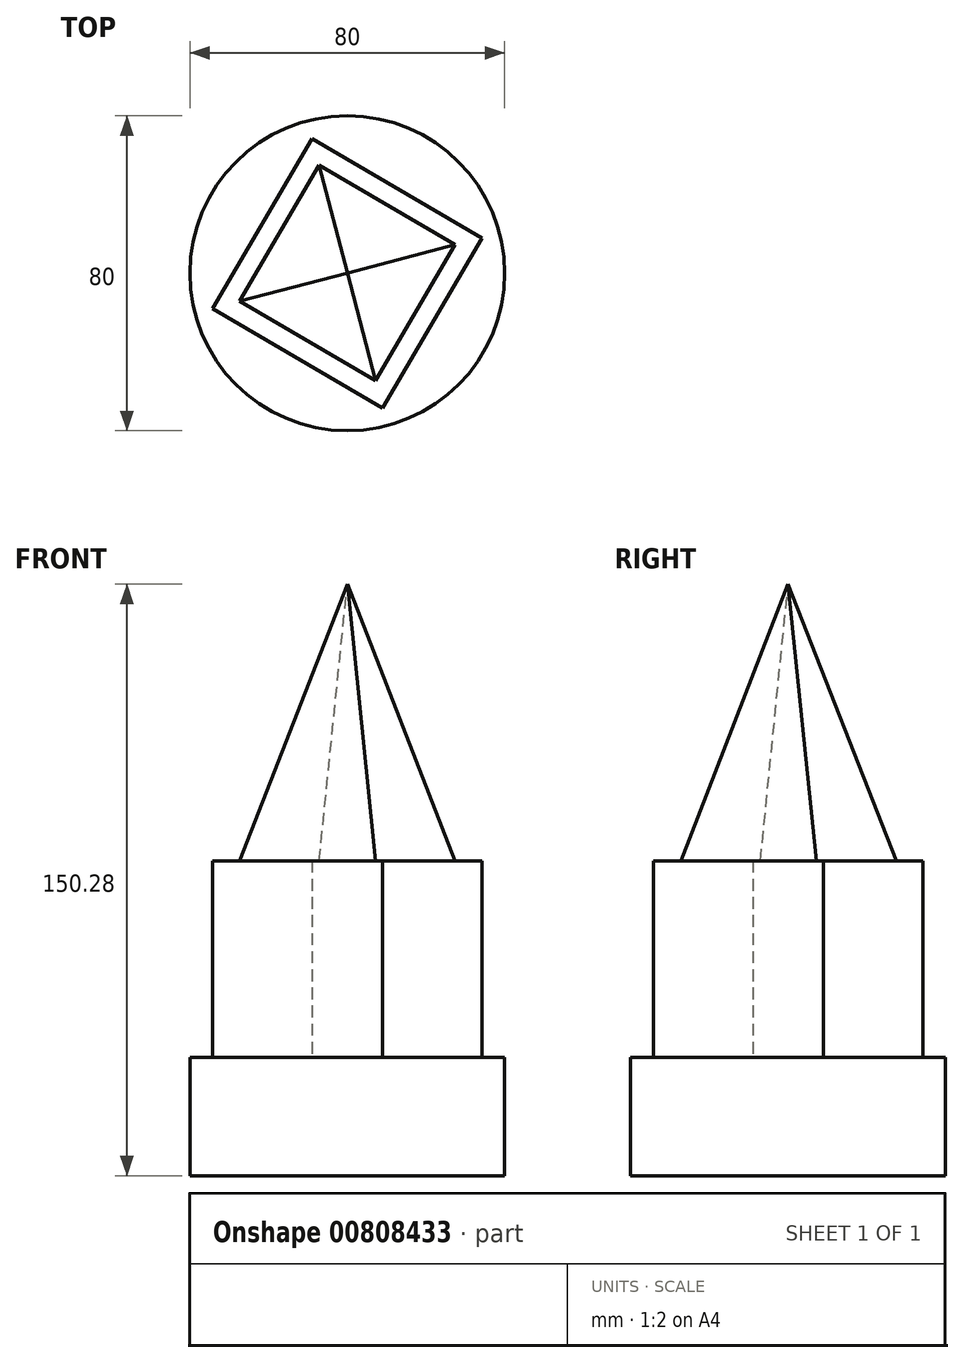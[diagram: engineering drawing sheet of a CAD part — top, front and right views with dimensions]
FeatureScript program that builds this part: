
annotation { "Feature Type Name" : "Feature", "Feature Type Description" : "" }
export const myFeature = defineFeature(function(context is Context, id is Id, definition is map)
    precondition{}
    {
        {
            var Q0;
            Q0=qCreatedBy(makeId("Top.planeOp"),FACE);
            var sketch = newSketch(context, id + "F0", { "sketchPlane" : qUnion([Q0])});
            skCircle(sketch, "E0", {"center": v(0, 0) * mm, "radius": 40 * mm});
            skSolve(sketch);
        }
        {
            var Q0;
            Q0 = qSketchRegion(id + "F0", true);
            extrude(context, id + "F1", {"entities" : qUnion([Q0]), "depth" : 30 * mm, "offsetDistance" : 25.4 * mm});
        }
        {
            var Q0;
            Q0=makeQuery(id+"F1.opExtrude","CAP_FACE",FACE,{"disambiguationData":[OSD([sQuery(id+"F0.wireOp",EDGE,"E0")])],"isStart":false});
            var sketch = newSketch(context, id + "F2", { "sketchPlane" : qUnion([Q0])});
            skCircle(sketch, "E1.cCircle", {"center": v(0, 0) * mm, "radius": 25 * mm, "construction": true});
            skLineSegment(sketch, "E1.0", {"start": v(-8.96, 34.2) * mm, "end": v(34.2, 8.96) * mm});
            skLineSegment(sketch, "E1.1", {"start": v(34.2, 8.96) * mm, "end": v(8.96, -34.2) * mm});
            skLineSegment(sketch, "E1.2", {"start": v(8.96, -34.2) * mm, "end": v(-34.2, -8.96) * mm});
            skLineSegment(sketch, "E1.3", {"start": v(-34.2, -8.96) * mm, "end": v(-8.96, 34.2) * mm});
            skPoint(sketch, "E1.0.midPoint", {"position": v(12.62, 21.58) * mm});
            skSolve(sketch);
        }
        {
            var Q0;
            Q0 = qSketchRegion(id + "F2", true);
            extrude(context, id + "F3", {"entities" : qUnion([Q0]), "operationType" : NewBodyOperationType.ADD, "depth" : 50 * mm, "offsetDistance" : 25.4 * mm});
        }
        {
            var Q0;
            Q0=makeQuery(id+"F3.opExtrude","CAP_FACE",FACE,{"disambiguationData":[OSD([sQuery(id+"F2.wireOp",EDGE,"E1.0"),sQuery(id+"F2.wireOp",EDGE,"E1.1"),sQuery(id+"F2.wireOp",EDGE,"E1.2"),sQuery(id+"F2.wireOp",EDGE,"E1.3")])],"isStart":false});
            var sketch = newSketch(context, id + "F4", { "sketchPlane" : qUnion([Q0])});
            skCircle(sketch, "E2.cCircle", {"center": v(0, 0) * mm, "radius": 20 * mm, "construction": true});
            skLineSegment(sketch, "E2.0", {"start": v(-27.38, -7.03) * mm, "end": v(-7.12, 27.46) * mm});
            skLineSegment(sketch, "E2.1", {"start": v(-7.12, 27.46) * mm, "end": v(27.37, 7.21) * mm});
            skLineSegment(sketch, "E2.2", {"start": v(27.37, 7.21) * mm, "end": v(7.12, -27.28) * mm});
            skLineSegment(sketch, "E2.3", {"start": v(7.12, -27.28) * mm, "end": v(-27.38, -7.03) * mm});
            skPoint(sketch, "E2.0.midPoint", {"position": v(-9.91, 17.37) * mm});
            skSolve(sketch);
        }
        {
            var Q0;
            Q0=qCreatedBy(makeId("Right.planeOp"),FACE);
            var sketch = newSketch(context, id + "F5", { "sketchPlane" : qUnion([Q0])});
            skLineSegment(sketch, "E3", {"start": v(0, 80.28) * mm, "end": v(0, 150.28) * mm});
            skSolve(sketch);
        }
        {
            var Q1;
            Q1=makeQuery(id+"F4.imprint","IMPRINT",FACE,{"disambiguationData":[TD([[makeQuery(id+"F4.imprint","IMPRINT",EDGE,{"derivedFrom":sQuery(id+"F4.wireOp",EDGE,"E2.0")}),-1.0]])]});
            var Q2;
            Q2=sQuery(id+"F5.wireOp",VERTEX,"E3.end");
            loft(context, id + "F6", {"operationType" : NewBodyOperationType.ADD, "sheetProfilesArray" : [{ "sheetProfileEntities" : qUnion([Q1]) }, { "sheetProfileEntities" : qUnion([Q2]) }]});
        }
    });
